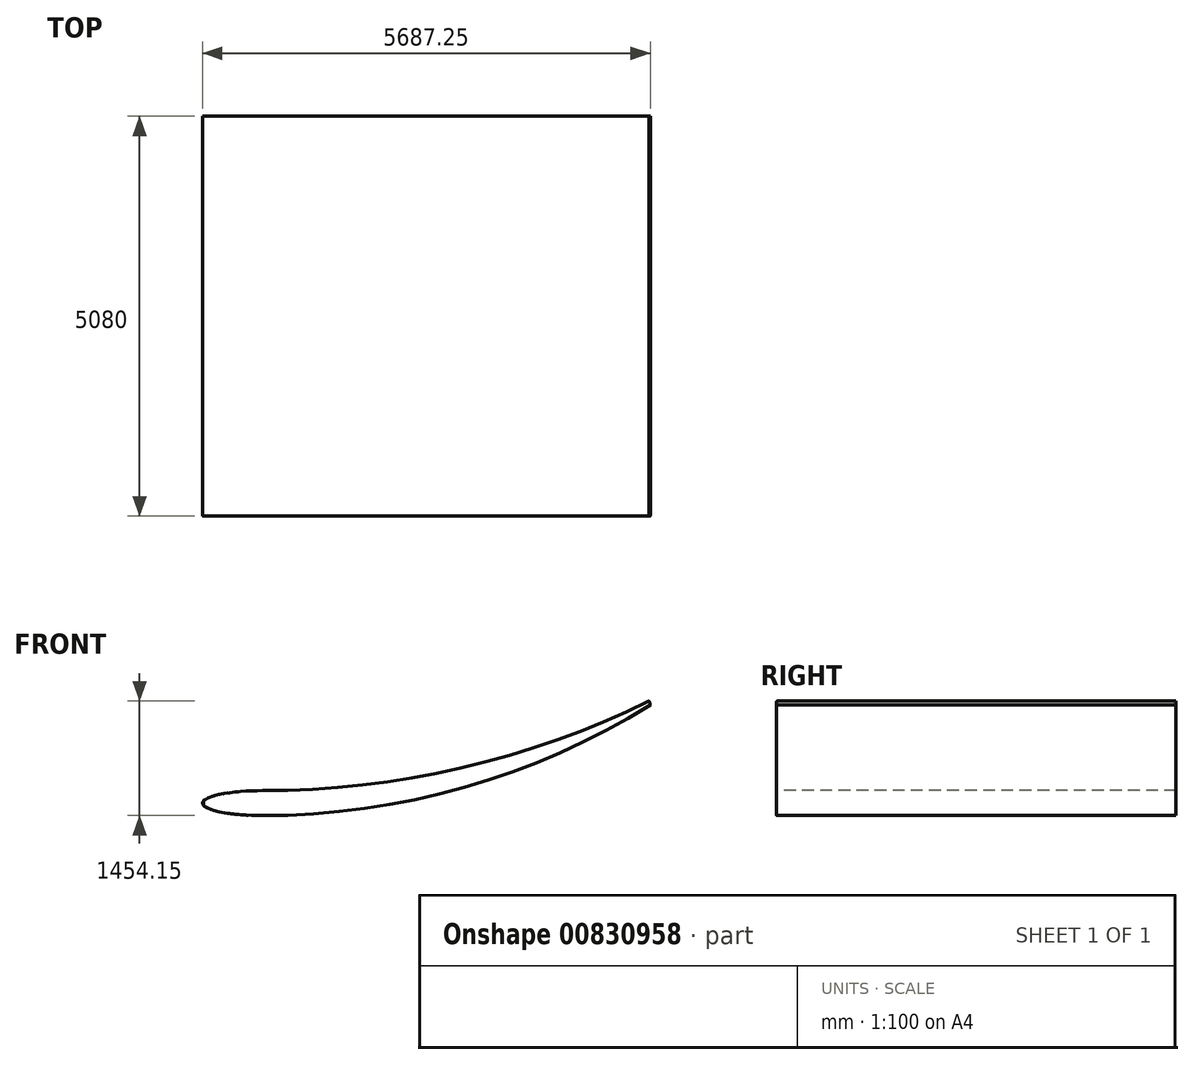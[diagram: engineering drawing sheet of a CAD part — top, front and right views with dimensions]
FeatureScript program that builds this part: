
annotation { "Feature Type Name" : "Feature", "Feature Type Description" : "" }
export const myFeature = defineFeature(function(context is Context, id is Id, definition is map)
    precondition{}
    {
        {
            var Q0;
            Q0=qCreatedBy(makeId("Front.planeOp"),FACE);
            var sketch = newSketch(context, id + "F0", { "sketchPlane" : qUnion([Q0])});
            skLineSegment(sketch, "E0", {"start": v(-587.22, 0) * mm, "end": v(174.78, 0) * mm, "construction": true});
            skLineSegment(sketch, "E1", {"start": v(174.78, 0) * mm, "end": v(5093.47, 1270) * mm, "construction": true});
            skLineSegment(sketch, "E2", {"start": v(174.78, 0) * mm, "end": v(174.78, -158.75) * mm, "construction": true});
            skLineSegment(sketch, "E3", {"start": v(174.78, 0) * mm, "end": v(174.78, 158.75) * mm, "construction": true});
            skEllipticalArc(sketch, "E4", {});
            skLineSegment(sketch, "E5", {"start": v(5093.47, 1270) * mm, "end": v(5086.9, 1295.4) * mm});
            skLineSegment(sketch, "E6", {"start": v(5093.47, 1270) * mm, "end": v(5100.03, 1244.6) * mm});
            skArc(sketch, "E7", {"start": v(174.78, 158.75) * mm, "mid": v(2695.74, 446.62) * mm, "end": v(5086.9, 1295.4) * mm});
            skArc(sketch, "E8", {"start": v(174.78, -158.75) * mm, "mid": v(2735.42, 198.93) * mm, "end": v(5100.03, 1244.6) * mm});
            const initialGuessF0  = {"E4": [0.17477889627863005, 0, -1, 0, 0.762, 0.15875, 4.71238898038469, 1.5707963267948966]};
            skSetInitialGuess(sketch, initialGuessF0);
            skSolve(sketch);
        }
        {
            var Q0;
            Q0 = qSketchRegion(id + "F0", true);
            extrude(context, id + "F1", {"entities" : qUnion([Q0]), "oppositeDirection" : true, "depth" : 5080 * mm, "offsetDistance" : 25.4 * mm});
        }
        {
            var Q0;
            Q0=makeQuery(id+"F1.opExtrude","CAP_EDGE",EDGE,{"disambiguationData":[OSD([sQuery(id+"F0.wireOp",EDGE,"E7")])],"isStart":true});
            var Q1;
            Q1=makeQuery(id+"F1.opExtrude","CAP_EDGE",EDGE,{"disambiguationData":[OSD([sQuery(id+"F0.wireOp",EDGE,"E4")])],"isStart":true});
            var Q2;
            Q2=makeQuery(id+"F1.opExtrude","CAP_EDGE",EDGE,{"disambiguationData":[OSD([sQuery(id+"F0.wireOp",EDGE,"E8")])],"isStart":true});
            fillet(context, id + "F2", {"entities" : qUnion([Q0, Q1, Q2]), "radius" : 12.7 * mm, "tangentPropagation" : true, "allowEdgeOverflow" : false});
        }
        {
            var Q0;
            Q0=makeQuery(id+"F1.opExtrude","SWEPT_BODY",BODY,{"disambiguationData":[OSD([sQuery(id+"F0.wireOp",EDGE,"E4"),sQuery(id+"F0.wireOp",EDGE,"E5"),sQuery(id+"F0.wireOp",EDGE,"E6"),sQuery(id+"F0.wireOp",EDGE,"E7"),sQuery(id+"F0.wireOp",EDGE,"E8")])]});
            transform(context, id + "F3", {"entities" : qUnion([Q0]), "transformType" : TransformType.TRANSLATION_3D, "dx" : 0 * mm, "dy" : 0 * mm, "dz" : 0 * mm, "makeCopy" : true});
        }
        {
            var Q0;
            Q0=makeQuery(id+"F3.opPattern","COPY",BODY,{"derivedFrom":makeQuery(id+"F1.opExtrude","SWEPT_BODY",BODY,{"disambiguationData":[OSD([sQuery(id+"F0.wireOp",EDGE,"E4"),sQuery(id+"F0.wireOp",EDGE,"E5"),sQuery(id+"F0.wireOp",EDGE,"E6"),sQuery(id+"F0.wireOp",EDGE,"E7"),sQuery(id+"F0.wireOp",EDGE,"E8")])]}),"instanceName":"1"});
            deleteBodies(context, id + "F4", {"entities" : qUnion([Q0])});
        }
        {
            var Q0;
            Q0=makeQuery(id+"F1.opExtrude","SWEPT_BODY",BODY,{"disambiguationData":[OSD([sQuery(id+"F0.wireOp",EDGE,"E4"),sQuery(id+"F0.wireOp",EDGE,"E5"),sQuery(id+"F0.wireOp",EDGE,"E6"),sQuery(id+"F0.wireOp",EDGE,"E7"),sQuery(id+"F0.wireOp",EDGE,"E8")])]});
            transform(context, id + "F5", {"entities" : qUnion([Q0]), "transformType" : TransformType.TRANSLATION_3D, "dx" : 0 * mm, "dy" : 0 * mm, "dz" : 993.14 * mm, "makeCopy" : true});
        }
        {
            var Q0;
            Q0=makeQuery(id+"F5.opPattern","COPY",BODY,{"derivedFrom":makeQuery(id+"F1.opExtrude","SWEPT_BODY",BODY,{"disambiguationData":[OSD([sQuery(id+"F0.wireOp",EDGE,"E4"),sQuery(id+"F0.wireOp",EDGE,"E5"),sQuery(id+"F0.wireOp",EDGE,"E6"),sQuery(id+"F0.wireOp",EDGE,"E7"),sQuery(id+"F0.wireOp",EDGE,"E8")])]}),"instanceName":"1"});
            deleteBodies(context, id + "F6", {"entities" : qUnion([Q0])});
        }
    });
